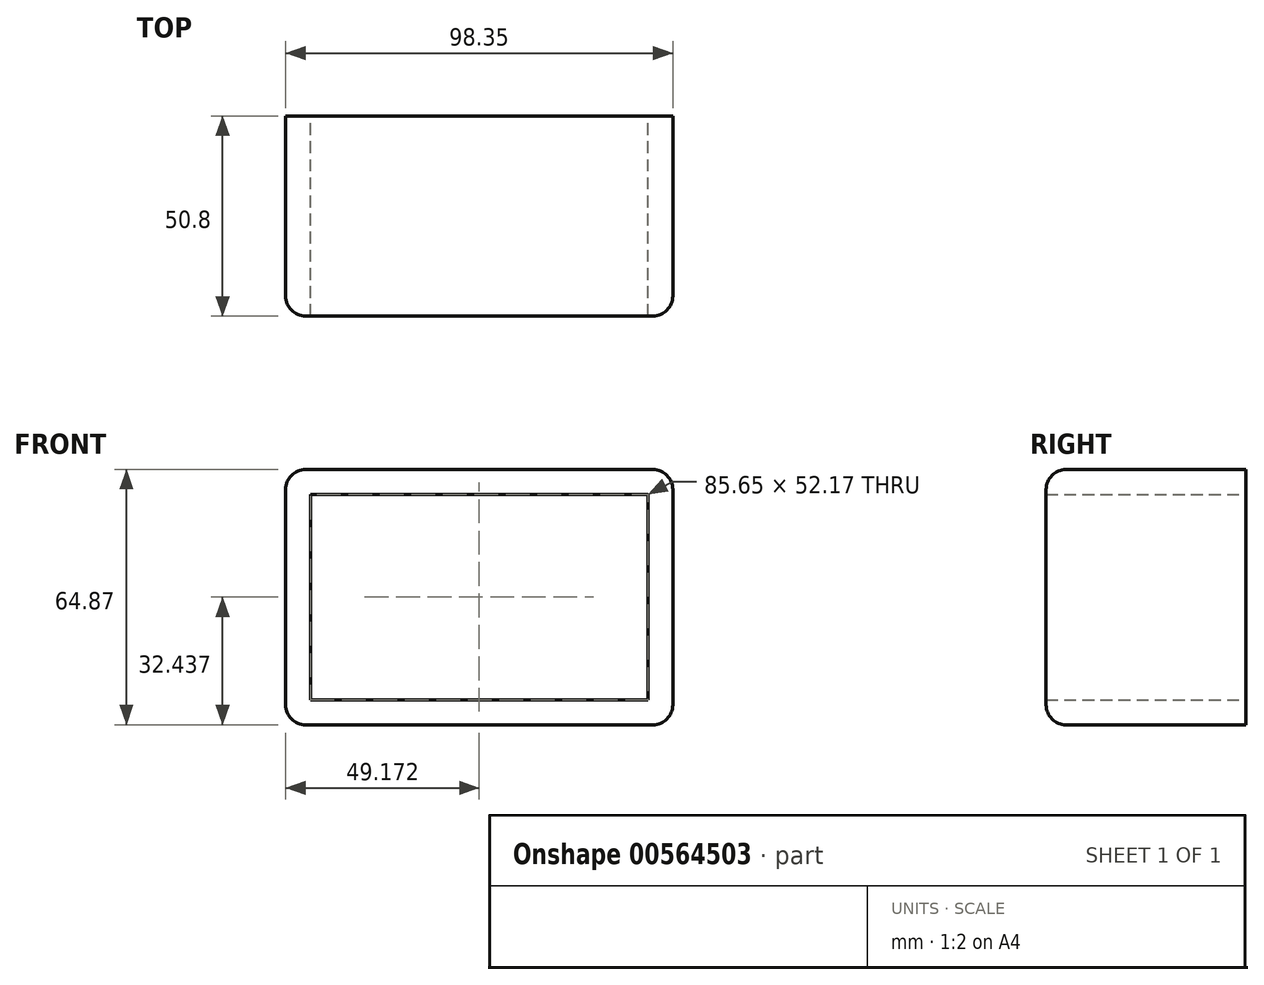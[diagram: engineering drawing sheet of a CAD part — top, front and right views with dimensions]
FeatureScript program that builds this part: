
annotation { "Feature Type Name" : "Feature", "Feature Type Description" : "" }
export const myFeature = defineFeature(function(context is Context, id is Id, definition is map)
    precondition{}
    {
        {
            var Q0;
            Q0=qCreatedBy(makeId("Front.planeOp"),FACE);
            var sketch = newSketch(context, id + "F0", { "sketchPlane" : qUnion([Q0])});
            skLineSegment(sketch, "E0.bottom", {"start": v(-42.71, 33.97) * mm, "end": v(42.94, 33.97) * mm});
            skLineSegment(sketch, "E0.top", {"start": v(-42.71, -18.2) * mm, "end": v(42.94, -18.2) * mm});
            skLineSegment(sketch, "E0.left", {"start": v(-42.71, 33.97) * mm, "end": v(-42.71, -18.2) * mm});
            skLineSegment(sketch, "E0.right", {"start": v(42.94, 33.97) * mm, "end": v(42.94, -18.2) * mm});
            skLineSegment(sketch, "E1.0", {"start": v(-49.06, 33.97) * mm, "end": v(-49.06, -18.2) * mm});
            skSolve(sketch);
        }
        {
            var Q0;
            Q0 = qSketchRegion(id + "F0", true);
            var sketch = newSketch(context, id + "F1", { "sketchPlane" : qUnion([Q0])});
            skLineSegment(sketch, "E2.0", {"start": v(-49.06, 40.32) * mm, "end": v(-49.06, -24.55) * mm});
            skLineSegment(sketch, "E2.1", {"start": v(-49.06, 40.32) * mm, "end": v(49.29, 40.32) * mm});
            skLineSegment(sketch, "E2.2", {"start": v(49.29, 40.32) * mm, "end": v(49.29, -24.55) * mm});
            skLineSegment(sketch, "E2.3", {"start": v(-49.06, -24.55) * mm, "end": v(49.29, -24.55) * mm});
            skSolve(sketch);
        }
        {
            var Q0;
            Q0=makeQuery(id+"F1.imprint","IMPRINT",FACE,{"disambiguationData":[TD([[makeQuery(id+"F1.imprint","IMPRINT",EDGE,{"derivedFrom":sQuery(id+"F1.wireOp",EDGE,"E2.0")}),1.0]])]});
            extrude(context, id + "F2", {"entities" : qUnion([Q0]), "depth" : 50.8 * mm, "offsetDistance" : 25.4 * mm});
        }
        {
            var Q0;
            Q0=makeQuery(id+"F2.opExtrude","CAP_EDGE",EDGE,{"disambiguationData":[OSD([sQuery(id+"F1.wireOp",EDGE,"E2.1")])],"isStart":false});
            var Q1;
            Q1=makeQuery(id+"F2.opExtrude","CAP_EDGE",EDGE,{"disambiguationData":[OSD([sQuery(id+"F1.wireOp",EDGE,"E2.2")])],"isStart":false});
            var Q2;
            Q2=makeQuery(id+"F2.opExtrude","CAP_EDGE",EDGE,{"disambiguationData":[OSD([sQuery(id+"F1.wireOp",EDGE,"E2.3")])],"isStart":false});
            var Q3;
            Q3=makeQuery(id+"F2.opExtrude","CAP_EDGE",EDGE,{"disambiguationData":[OSD([sQuery(id+"F1.wireOp",EDGE,"E2.0")])],"isStart":false});
            fillet(context, id + "F3", {"entities" : qUnion([Q0, Q1, Q2, Q3]), "radius" : 5.08 * mm, "tangentPropagation" : true, "allowEdgeOverflow" : false});
        }
        {
            var Q0;
            Q0=makeQuery(id+"F2.opExtrude","SWEPT_EDGE",EDGE,{"disambiguationData":[OSD([sQuery(id+"F1.wireOp",EDGE,"E2.1"),sQuery(id+"F1.wireOp",EDGE,"E2.2")])]});
            var Q1;
            Q1=makeQuery(id+"F2.opExtrude","SWEPT_EDGE",EDGE,{"disambiguationData":[OSD([sQuery(id+"F1.wireOp",EDGE,"E2.2"),sQuery(id+"F1.wireOp",EDGE,"E2.3")])]});
            var Q2;
            Q2=makeQuery(id+"F2.opExtrude","SWEPT_EDGE",EDGE,{"disambiguationData":[OSD([sQuery(id+"F1.wireOp",EDGE,"E2.0"),sQuery(id+"F1.wireOp",EDGE,"E2.3")])]});
            fillet(context, id + "F4", {"entities" : qUnion([Q0, Q1, Q2]), "radius" : 5.08 * mm, "tangentPropagation" : true, "allowEdgeOverflow" : false});
        }
        {
            var Q0;
            Q0=makeQuery(id+"F2.opExtrude","SWEPT_EDGE",EDGE,{"disambiguationData":[OSD([sQuery(id+"F1.wireOp",EDGE,"E2.0"),sQuery(id+"F1.wireOp",EDGE,"E2.1")])]});
            fillet(context, id + "F5", {"entities" : qUnion([Q0]), "radius" : 5.08 * mm, "tangentPropagation" : true, "allowEdgeOverflow" : false});
        }
    });
